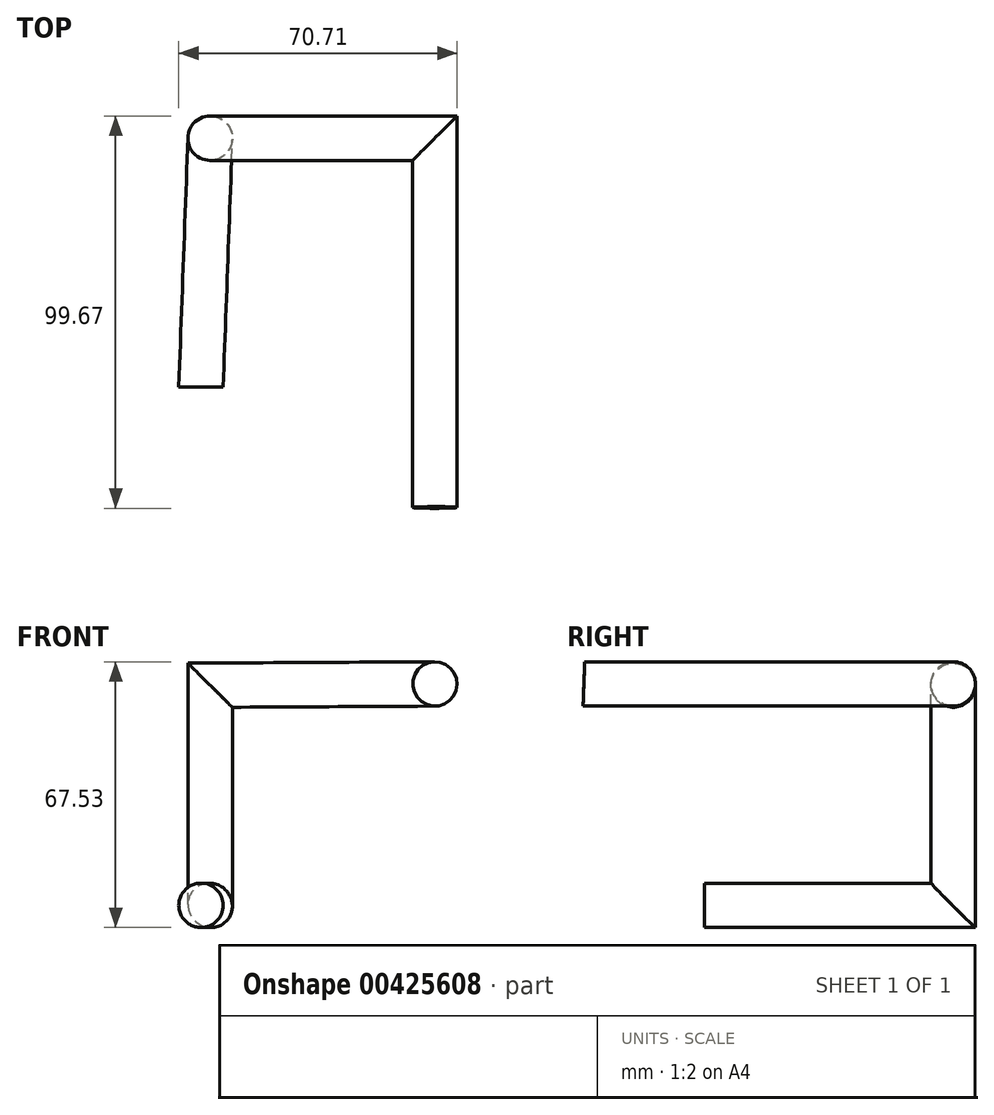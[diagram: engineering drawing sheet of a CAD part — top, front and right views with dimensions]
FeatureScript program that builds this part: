
annotation { "Feature Type Name" : "Feature", "Feature Type Description" : "" }
export const myFeature = defineFeature(function(context is Context, id is Id, definition is map)
    precondition{}
    {
        {
            var Q0;
            Q0=qCreatedBy(makeId("Top.planeOp"),FACE);
            var sketch = newSketch(context, id + "F0", { "sketchPlane" : qUnion([Q0])});
            skLineSegment(sketch, "E0", {"start": v(-59.43, -63.2) * mm, "end": v(-57.1, 0) * mm});
            skSolve(sketch);
        }
        {
            var Q0;
            Q0=qCreatedBy(makeId("Front.planeOp"),FACE);
            var sketch = newSketch(context, id + "F1", { "sketchPlane" : qUnion([Q0])});
            skLineSegment(sketch, "E1", {"start": v(-57.1, 0) * mm, "end": v(-57.1, 55.93) * mm});
            skSolve(sketch);
        }
        {
            var Q0;
            Q0=qCreatedBy(makeId("Front.planeOp"),FACE);
            var sketch = newSketch(context, id + "F2", { "sketchPlane" : qUnion([Q0])});
            skLineSegment(sketch, "E2", {"start": v(-57.1, 55.93) * mm, "end": v(0, 56.25) * mm});
            skSolve(sketch);
        }
        {
            var Q0;
            Q0=qCreatedBy(makeId("Right.planeOp"),FACE);
            var sketch = newSketch(context, id + "F3", { "sketchPlane" : qUnion([Q0])});
            skLineSegment(sketch, "E3", {"start": v(0, 56.25) * mm, "end": v(-93.83, 56.25) * mm});
            skSolve(sketch);
        }
        {
            var Q0;
            Q0=qCreatedBy(makeId("Front.planeOp"),FACE);
            var Q1;
            Q1=sQuery(id+"F0.wireOp",VERTEX,"E0.start");
            cPlane(context, id + "F4", {"entities" : qUnion([Q0, Q1]), "cplaneType" : CPlaneType.PLANE_POINT, "offset" : 64 * mm, "width" : 152.4 * mm, "height" : 152.4 * mm});
        }
        {
            var Q0;
            Q0=qCreatedBy(id+"F4.planeOp",FACE);
            var sketch = newSketch(context, id + "F5", { "sketchPlane" : qUnion([Q0])});
            skCircle(sketch, "E4", {"center": v(-59.43, 0) * mm, "radius": 5.64 * mm});
            skSolve(sketch);
        }
        {
            var Q0;
            Q0=makeQuery(id+"F5.imprint","IMPRINT",FACE,{"disambiguationData":[TD([[makeQuery(id+"F5.imprint","IMPRINT",EDGE,{"derivedFrom":sQuery(id+"F5.wireOp",EDGE,"E4")}),1.0]])]});
            var Q1;
            Q1=sQuery(id+"F0.wireOp",EDGE,"E0");
            var Q2;
            Q2=sQuery(id+"F1.wireOp",EDGE,"E1");
            var Q3;
            Q3=sQuery(id+"F2.wireOp",EDGE,"E2");
            var Q4;
            Q4=sQuery(id+"F3.wireOp",EDGE,"E3");
            sweep(context, id + "F6", {"profiles" : qUnion([Q0]), "path" : qUnion([Q1, Q2, Q3, Q4])});
        }
    });
